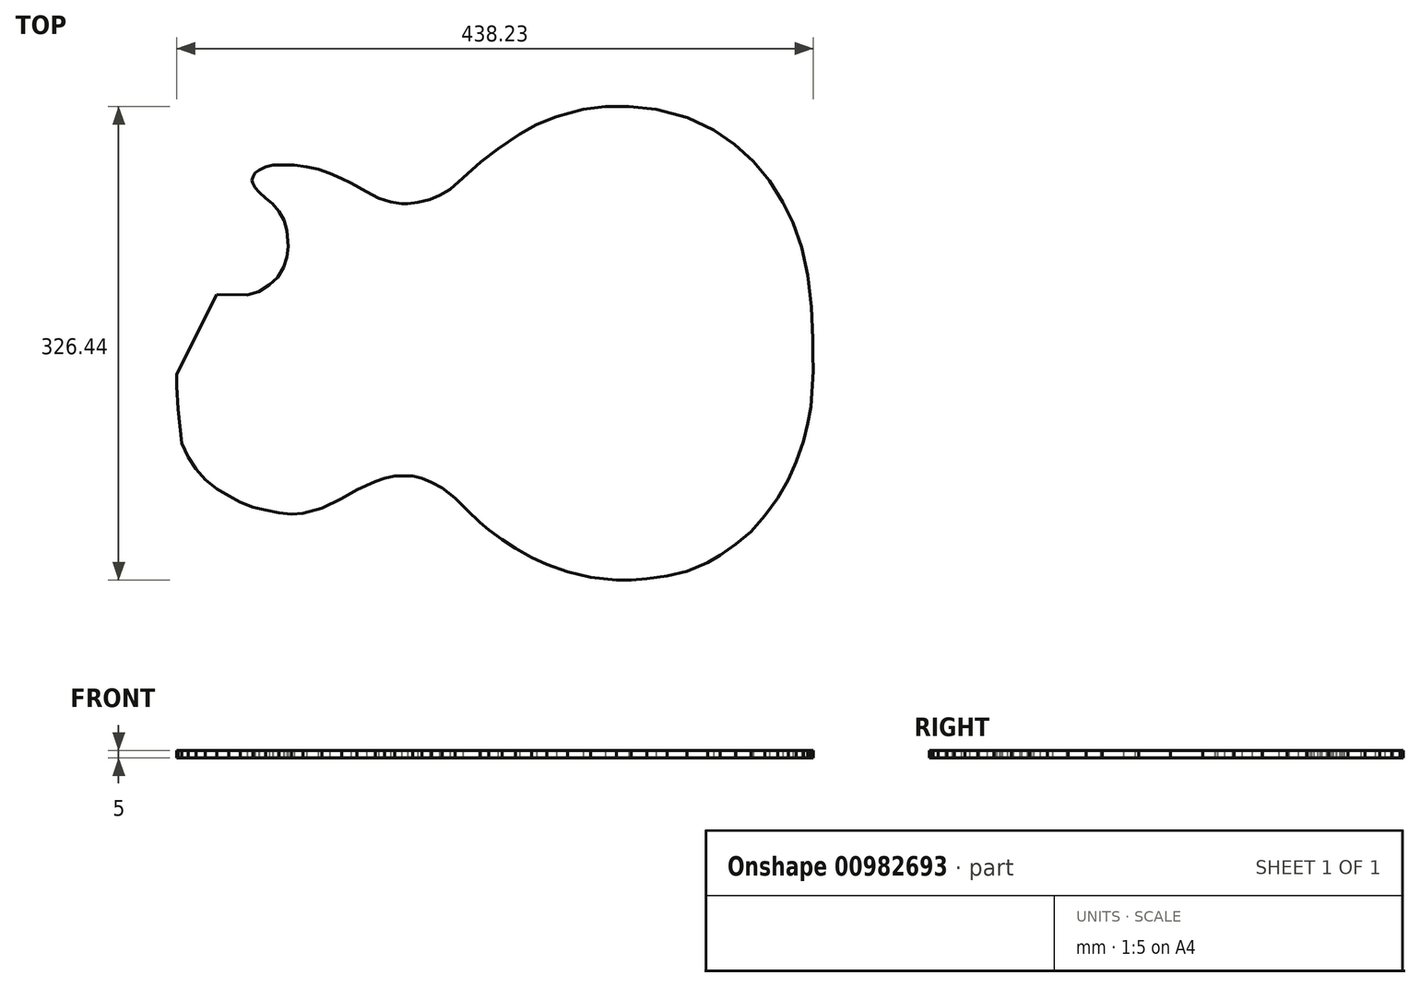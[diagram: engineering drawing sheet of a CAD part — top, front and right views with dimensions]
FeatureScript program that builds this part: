
annotation { "Feature Type Name" : "Feature", "Feature Type Description" : "" }
export const myFeature = defineFeature(function(context is Context, id is Id, definition is map)
    precondition{}
    {
        {
            var Q0;
            Q0=qCreatedBy(makeId("Top.planeOp"),FACE);
            var sketch = newSketch(context, id + "F0", { "sketchPlane" : qUnion([Q0])});
            skLineSegment(sketch, "E0", {"start": v(241.87, -9.5) * mm, "end": v(241.87, 1.22) * mm});
            skLineSegment(sketch, "E1", {"start": v(241.87, 1.22) * mm, "end": v(240.9, 23.4) * mm});
            skLineSegment(sketch, "E2", {"start": v(240.9, 23.4) * mm, "end": v(238.19, 45.15) * mm});
            skLineSegment(sketch, "E3", {"start": v(238.19, 45.15) * mm, "end": v(234.08, 64.4) * mm});
            skLineSegment(sketch, "E4", {"start": v(234.08, 64.4) * mm, "end": v(228.13, 81.5) * mm});
            skLineSegment(sketch, "E5", {"start": v(228.13, 81.5) * mm, "end": v(221.2, 95.35) * mm});
            skLineSegment(sketch, "E6", {"start": v(221.2, 95.35) * mm, "end": v(211.79, 110.28) * mm});
            skLineSegment(sketch, "E7", {"start": v(211.79, 110.28) * mm, "end": v(200.65, 123.59) * mm});
            skLineSegment(sketch, "E8", {"start": v(200.65, 123.59) * mm, "end": v(187.77, 135.38) * mm});
            skLineSegment(sketch, "E9", {"start": v(187.77, 135.38) * mm, "end": v(173.6, 145.23) * mm});
            skLineSegment(sketch, "E10", {"start": v(173.6, 145.23) * mm, "end": v(155.31, 153.78) * mm});
            skLineSegment(sketch, "E11", {"start": v(155.31, 153.78) * mm, "end": v(133.9, 159.4) * mm});
            skLineSegment(sketch, "E12", {"start": v(133.9, 159.4) * mm, "end": v(115.17, 161.46) * mm});
            skLineSegment(sketch, "E13", {"start": v(115.17, 161.46) * mm, "end": v(98.73, 161.46) * mm});
            skLineSegment(sketch, "E14", {"start": v(98.73, 161.46) * mm, "end": v(83.69, 159.4) * mm});
            skLineSegment(sketch, "E15", {"start": v(83.69, 159.4) * mm, "end": v(65.08, 154.53) * mm});
            skLineSegment(sketch, "E16", {"start": v(65.08, 154.53) * mm, "end": v(51.56, 148.9) * mm});
            skLineSegment(sketch, "E17", {"start": v(51.56, 148.9) * mm, "end": v(39.65, 142.3) * mm});
            skLineSegment(sketch, "E18", {"start": v(39.65, 142.3) * mm, "end": v(24.83, 132.35) * mm});
            skLineSegment(sketch, "E19", {"start": v(24.83, 132.35) * mm, "end": v(13.15, 123.37) * mm});
            skLineSegment(sketch, "E20", {"start": v(13.15, 123.37) * mm, "end": v(0.92, 112.23) * mm});
            skLineSegment(sketch, "E21", {"start": v(0.92, 112.23) * mm, "end": v(-8.28, 104.22) * mm});
            skLineSegment(sketch, "E22", {"start": v(-8.28, 104.22) * mm, "end": v(-15.42, 100) * mm});
            skLineSegment(sketch, "E23", {"start": v(-15.42, 100) * mm, "end": v(-22.02, 97.4) * mm});
            skLineSegment(sketch, "E24", {"start": v(-22.02, 97.4) * mm, "end": v(-30.35, 95.35) * mm});
            skLineSegment(sketch, "E25", {"start": v(-30.35, 95.35) * mm, "end": v(-37.23, 94.41) * mm});
            skLineSegment(sketch, "E26", {"start": v(-37.23, 94.41) * mm, "end": v(-41.61, 94.41) * mm});
            skLineSegment(sketch, "E27", {"start": v(-41.61, 94.41) * mm, "end": v(-49.08, 95.78) * mm});
            skLineSegment(sketch, "E28", {"start": v(-49.08, 95.78) * mm, "end": v(-57.2, 98.27) * mm});
            skLineSegment(sketch, "E29", {"start": v(-57.2, 98.27) * mm, "end": v(-65.74, 102.6) * mm});
            skLineSegment(sketch, "E30", {"start": v(-65.74, 102.6) * mm, "end": v(-76.46, 108.66) * mm});
            skLineSegment(sketch, "E31", {"start": v(-76.46, 108.66) * mm, "end": v(-83.17, 111.9) * mm});
            skLineSegment(sketch, "E32", {"start": v(-83.17, 111.9) * mm, "end": v(-91.06, 115.37) * mm});
            skLineSegment(sketch, "E33", {"start": v(-91.06, 115.37) * mm, "end": v(-99.07, 118.29) * mm});
            skLineSegment(sketch, "E34", {"start": v(-99.07, 118.29) * mm, "end": v(-106.86, 119.91) * mm});
            skLineSegment(sketch, "E35", {"start": v(-106.86, 119.91) * mm, "end": v(-115.52, 121) * mm});
            skLineSegment(sketch, "E36", {"start": v(-115.52, 121) * mm, "end": v(-123.64, 121) * mm});
            skLineSegment(sketch, "E37", {"start": v(-123.64, 121) * mm, "end": v(-129.91, 121) * mm});
            skLineSegment(sketch, "E38", {"start": v(-129.91, 121) * mm, "end": v(-135.21, 119.7) * mm});
            skLineSegment(sketch, "E39", {"start": v(-135.21, 119.7) * mm, "end": v(-139.65, 117.75) * mm});
            skLineSegment(sketch, "E40", {"start": v(-139.65, 117.75) * mm, "end": v(-142.36, 115.58) * mm});
            skLineSegment(sketch, "E41", {"start": v(-142.36, 115.58) * mm, "end": v(-143.66, 113.2) * mm});
            skLineSegment(sketch, "E42", {"start": v(-143.66, 113.2) * mm, "end": v(-144.74, 110.6) * mm});
            skLineSegment(sketch, "E43", {"start": v(-144.74, 110.6) * mm, "end": v(-143.98, 108.66) * mm});
            skLineSegment(sketch, "E44", {"start": v(-143.98, 108.66) * mm, "end": v(-142.46, 105.41) * mm});
            skLineSegment(sketch, "E45", {"start": v(-142.46, 105.41) * mm, "end": v(-139.54, 102.38) * mm});
            skLineSegment(sketch, "E46", {"start": v(-139.54, 102.38) * mm, "end": v(-135.21, 98.38) * mm});
            skLineSegment(sketch, "E47", {"start": v(-135.21, 98.38) * mm, "end": v(-130.45, 94.38) * mm});
            skLineSegment(sketch, "E48", {"start": v(-130.45, 94.38) * mm, "end": v(-125.8, 89.08) * mm});
            skLineSegment(sketch, "E49", {"start": v(-125.8, 89.08) * mm, "end": v(-122.34, 82.9) * mm});
            skLineSegment(sketch, "E50", {"start": v(-122.34, 82.9) * mm, "end": v(-120.5, 75.88) * mm});
            skLineSegment(sketch, "E51", {"start": v(-120.5, 75.88) * mm, "end": v(-119.55, 65) * mm});
            skLineSegment(sketch, "E52", {"start": v(-119.55, 65) * mm, "end": v(-120.52, 57.54) * mm});
            skLineSegment(sketch, "E53", {"start": v(-120.52, 57.54) * mm, "end": v(-121.78, 53.83) * mm});
            skLineSegment(sketch, "E54", {"start": v(-122.9, 50.5) * mm, "end": v(-127.02, 43.7) * mm});
            skLineSegment(sketch, "E55", {"start": v(-127.02, 43.7) * mm, "end": v(-132.75, 38.5) * mm});
            skLineSegment(sketch, "E56", {"start": v(-132.75, 38.5) * mm, "end": v(-140, 33.74) * mm});
            skLineSegment(sketch, "E57", {"start": v(-140, 33.74) * mm, "end": v(-147.93, 31.7) * mm});
            skLineSegment(sketch, "E58", {"start": v(-168.91, 31.93) * mm, "end": v(-196.33, -23.07) * mm});
            skLineSegment(sketch, "E59", {"start": v(-196.33, -23.07) * mm, "end": v(-196.33, -31.18) * mm});
            skLineSegment(sketch, "E60", {"start": v(-196.33, -31.18) * mm, "end": v(-195.5, -47.01) * mm});
            skLineSegment(sketch, "E61", {"start": v(-192.82, -70.53) * mm, "end": v(-188.49, -80.05) * mm});
            skLineSegment(sketch, "E62", {"start": v(-188.49, -80.05) * mm, "end": v(-182.97, -88.6) * mm});
            skLineSegment(sketch, "E63", {"start": v(-182.97, -88.6) * mm, "end": v(-176.58, -95.84) * mm});
            skLineSegment(sketch, "E64", {"start": v(-176.58, -95.84) * mm, "end": v(-168.91, -102.07) * mm});
            skLineSegment(sketch, "E65", {"start": v(-168.91, -102.07) * mm, "end": v(-160.5, -106.98) * mm});
            skLineSegment(sketch, "E66", {"start": v(-160.5, -106.98) * mm, "end": v(-152.64, -111.3) * mm});
            skLineSegment(sketch, "E67", {"start": v(-152.64, -111.3) * mm, "end": v(-143.87, -114.76) * mm});
            skLineSegment(sketch, "E68", {"start": v(-143.87, -114.76) * mm, "end": v(-135.21, -116.7) * mm});
            skLineSegment(sketch, "E69", {"start": v(-135.21, -116.7) * mm, "end": v(-125.92, -118.58) * mm});
            skLineSegment(sketch, "E70", {"start": v(-125.92, -118.58) * mm, "end": v(-117.41, -119.4) * mm});
            skLineSegment(sketch, "E71", {"start": v(-117.41, -119.4) * mm, "end": v(-109.47, -118.88) * mm});
            skLineSegment(sketch, "E72", {"start": v(-109.47, -118.88) * mm, "end": v(-96.26, -115.28) * mm});
            skLineSegment(sketch, "E73", {"start": v(-96.26, -115.28) * mm, "end": v(-82.63, -108.9) * mm});
            skLineSegment(sketch, "E74", {"start": v(-82.63, -108.9) * mm, "end": v(-72.35, -102.73) * mm});
            skLineSegment(sketch, "E75", {"start": v(-72.35, -102.73) * mm, "end": v(-59.47, -97.1) * mm});
            skLineSegment(sketch, "E76", {"start": v(-59.47, -97.1) * mm, "end": v(-53.09, -94.72) * mm});
            skLineSegment(sketch, "E77", {"start": v(-53.09, -94.72) * mm, "end": v(-46.27, -93.2) * mm});
            skLineSegment(sketch, "E78", {"start": v(-46.27, -93.2) * mm, "end": v(-39.78, -93.2) * mm});
            skLineSegment(sketch, "E79", {"start": v(-39.78, -93.2) * mm, "end": v(-33.72, -93.2) * mm});
            skLineSegment(sketch, "E80", {"start": v(-33.72, -93.2) * mm, "end": v(-27.55, -94.83) * mm});
            skLineSegment(sketch, "E81", {"start": v(-27.55, -94.83) * mm, "end": v(-20.73, -97.54) * mm});
            skLineSegment(sketch, "E82", {"start": v(-20.73, -97.54) * mm, "end": v(-13.7, -101.32) * mm});
            skLineSegment(sketch, "E83", {"start": v(-13.7, -101.32) * mm, "end": v(-4.72, -108.47) * mm});
            skLineSegment(sketch, "E84", {"start": v(-4.72, -108.47) * mm, "end": v(3.62, -116.58) * mm});
            skLineSegment(sketch, "E85", {"start": v(3.62, -116.58) * mm, "end": v(12.38, -125.13) * mm});
            skLineSegment(sketch, "E86", {"start": v(12.38, -125.13) * mm, "end": v(18.66, -130.43) * mm});
            skLineSegment(sketch, "E87", {"start": v(18.66, -130.43) * mm, "end": v(27.64, -137.14) * mm});
            skLineSegment(sketch, "E88", {"start": v(27.64, -137.14) * mm, "end": v(36.84, -142.98) * mm});
            skLineSegment(sketch, "E89", {"start": v(36.84, -142.98) * mm, "end": v(48.1, -149.25) * mm});
            skLineSegment(sketch, "E90", {"start": v(48.1, -149.25) * mm, "end": v(58.7, -154.12) * mm});
            skLineSegment(sketch, "E91", {"start": v(58.7, -154.12) * mm, "end": v(72.76, -159.2) * mm});
            skLineSegment(sketch, "E92", {"start": v(72.76, -159.2) * mm, "end": v(88.56, -163) * mm});
            skLineSegment(sketch, "E93", {"start": v(88.56, -163) * mm, "end": v(98.3, -164.08) * mm});
            skLineSegment(sketch, "E94", {"start": v(98.3, -164.08) * mm, "end": v(106.4, -164.98) * mm});
            skLineSegment(sketch, "E95", {"start": v(106.4, -164.98) * mm, "end": v(116.7, -164.98) * mm});
            skLineSegment(sketch, "E96", {"start": v(116.7, -164.98) * mm, "end": v(127.4, -164.08) * mm});
            skLineSegment(sketch, "E97", {"start": v(127.4, -164.08) * mm, "end": v(141.37, -162.24) * mm});
            skLineSegment(sketch, "E98", {"start": v(141.37, -162.24) * mm, "end": v(155, -158.78) * mm});
            skLineSegment(sketch, "E99", {"start": v(155, -158.78) * mm, "end": v(169.4, -152.82) * mm});
            skLineSegment(sketch, "E100", {"start": v(169.4, -152.82) * mm, "end": v(178.05, -147.74) * mm});
            skLineSegment(sketch, "E101", {"start": v(178.05, -147.74) * mm, "end": v(188.66, -140.27) * mm});
            skLineSegment(sketch, "E102", {"start": v(188.66, -140.27) * mm, "end": v(199.05, -131.62) * mm});
            skLineSegment(sketch, "E103", {"start": v(199.05, -131.62) * mm, "end": v(208.57, -120.47) * mm});
            skLineSegment(sketch, "E104", {"start": v(208.57, -120.47) * mm, "end": v(217.55, -108.36) * mm});
            skLineSegment(sketch, "E105", {"start": v(217.55, -108.36) * mm, "end": v(224.9, -95.8) * mm});
            skLineSegment(sketch, "E106", {"start": v(224.9, -95.8) * mm, "end": v(230.43, -83.47) * mm});
            skLineSegment(sketch, "E107", {"start": v(230.43, -83.47) * mm, "end": v(235.4, -69.2) * mm});
            skLineSegment(sketch, "E108", {"start": v(235.4, -69.2) * mm, "end": v(238.33, -56.86) * mm});
            skLineSegment(sketch, "E109", {"start": v(238.33, -56.86) * mm, "end": v(240.6, -45.6) * mm});
            skLineSegment(sketch, "E110", {"start": v(240.6, -45.6) * mm, "end": v(241.9, -20.83) * mm});
            skLineSegment(sketch, "E111", {"start": v(241.9, -20.83) * mm, "end": v(241.87, -9.5) * mm});
            skLineSegment(sketch, "E112", {"start": v(-168.91, 31.93) * mm, "end": v(-134.22, 31.56) * mm});
            skLineSegment(sketch, "E113", {"start": v(-113.15, 31.33) * mm, "end": v(-113.74, -23.8) * mm});
            skLineSegment(sketch, "E114", {"start": v(-196.33, -23.07) * mm, "end": v(-113.74, -23.8) * mm});
            skLineSegment(sketch, "E115.bottom", {"start": v(-105.24, 38.33) * mm, "end": v(-68.24, 38.33) * mm});
            skLineSegment(sketch, "E115.top", {"start": v(-105.24, -30.67) * mm, "end": v(-68.24, -30.67) * mm});
            skLineSegment(sketch, "E115.left", {"start": v(-105.24, 38.33) * mm, "end": v(-105.24, -30.67) * mm});
            skLineSegment(sketch, "E115.right", {"start": v(-68.24, 38.33) * mm, "end": v(-68.24, -30.67) * mm});
            skLineSegment(sketch, "E116.bottom", {"start": v(-2.24, 38.33) * mm, "end": v(34.76, 38.33) * mm});
            skLineSegment(sketch, "E116.top", {"start": v(-2.24, -30.67) * mm, "end": v(34.76, -30.67) * mm});
            skLineSegment(sketch, "E116.left", {"start": v(-2.24, 38.33) * mm, "end": v(-2.24, -30.67) * mm});
            skLineSegment(sketch, "E116.right", {"start": v(34.76, 38.33) * mm, "end": v(34.76, -30.67) * mm});
            skLineSegment(sketch, "E117.top", {"start": v(109.76, -47.01) * mm, "end": v(-195.5, -47.01) * mm});
            skLineSegment(sketch, "E117.left", {"start": v(109.76, 52.99) * mm, "end": v(109.76, -47.01) * mm});
            skLineSegment(sketch, "E118", {"start": v(-195.5, -47.01) * mm, "end": v(-192.82, -70.53) * mm});
            skLineSegment(sketch, "E119", {"start": v(-121.78, 53.83) * mm, "end": v(-122.9, 50.5) * mm});
            skLineSegment(sketch, "E120", {"start": v(-121.78, 53.83) * mm, "end": v(109.76, 52.99) * mm});
            skLineSegment(sketch, "E121.2", {"start": v(-123.11, 40.48) * mm, "end": v(-129.68, 34.53) * mm});
            skLineSegment(sketch, "E121.3", {"start": v(-118.34, 48.4) * mm, "end": v(-123.11, 40.48) * mm});
            skLineSegment(sketch, "E121.4", {"start": v(-117.04, 52.22) * mm, "end": v(-118.34, 48.4) * mm});
            skLineSegment(sketch, "E121.5", {"start": v(-115.63, 56.4) * mm, "end": v(-117.04, 52.22) * mm});
            skLineSegment(sketch, "E121.6", {"start": v(-114.52, 64.9) * mm, "end": v(-115.63, 56.4) * mm});
            skLineSegment(sketch, "E121.7", {"start": v(-115.55, 76.73) * mm, "end": v(-114.52, 64.9) * mm});
            skLineSegment(sketch, "E121.8", {"start": v(-117.66, 84.8) * mm, "end": v(-115.55, 76.73) * mm});
            skLineSegment(sketch, "E121.9", {"start": v(-121.7, 91.98) * mm, "end": v(-117.66, 84.8) * mm});
            skLineSegment(sketch, "E121.10", {"start": v(-126.95, 97.96) * mm, "end": v(-121.7, 91.98) * mm});
            skLineSegment(sketch, "E121.11", {"start": v(-131.9, 102.13) * mm, "end": v(-126.95, 97.96) * mm});
            skLineSegment(sketch, "E121.12", {"start": v(-136.04, 105.96) * mm, "end": v(-131.9, 102.13) * mm});
            skLineSegment(sketch, "E121.13", {"start": v(-138.29, 108.28) * mm, "end": v(-136.04, 105.96) * mm});
            skLineSegment(sketch, "E121.14", {"start": v(-139.34, 110.55) * mm, "end": v(-138.29, 108.28) * mm});
            skLineSegment(sketch, "E121.15", {"start": v(-139.14, 111.04) * mm, "end": v(-139.34, 110.55) * mm});
            skLineSegment(sketch, "E121.16", {"start": v(-138.45, 112.3) * mm, "end": v(-139.14, 111.04) * mm});
            skLineSegment(sketch, "E121.17", {"start": v(-137.04, 113.43) * mm, "end": v(-138.45, 112.3) * mm});
            skLineSegment(sketch, "E121.18", {"start": v(-133.6, 114.94) * mm, "end": v(-137.04, 113.43) * mm});
            skLineSegment(sketch, "E121.19", {"start": v(-129.3, 116) * mm, "end": v(-133.6, 114.94) * mm});
            skLineSegment(sketch, "E121.20", {"start": v(-123.64, 116) * mm, "end": v(-129.3, 116) * mm});
            skLineSegment(sketch, "E121.21", {"start": v(-115.83, 116) * mm, "end": v(-123.64, 116) * mm});
            skLineSegment(sketch, "E121.22", {"start": v(-107.68, 114.98) * mm, "end": v(-115.83, 116) * mm});
            skLineSegment(sketch, "E121.23", {"start": v(-100.45, 113.47) * mm, "end": v(-107.68, 114.98) * mm});
            skLineSegment(sketch, "E121.24", {"start": v(-92.93, 110.72) * mm, "end": v(-100.45, 113.47) * mm});
            skLineSegment(sketch, "E121.25", {"start": v(-85.26, 107.36) * mm, "end": v(-92.93, 110.72) * mm});
            skLineSegment(sketch, "E121.26", {"start": v(-78.78, 104.23) * mm, "end": v(-85.26, 107.36) * mm});
            skLineSegment(sketch, "E121.27", {"start": v(-68.1, 98.2) * mm, "end": v(-78.78, 104.23) * mm});
            skLineSegment(sketch, "E121.28", {"start": v(-59.07, 93.62) * mm, "end": v(-68.1, 98.2) * mm});
            skLineSegment(sketch, "E121.29", {"start": v(-50.27, 90.92) * mm, "end": v(-59.07, 93.62) * mm});
            skLineSegment(sketch, "E121.30", {"start": v(-42.07, 89.41) * mm, "end": v(-50.27, 90.92) * mm});
            skLineSegment(sketch, "E121.31", {"start": v(-36.9, 89.41) * mm, "end": v(-42.07, 89.41) * mm});
            skLineSegment(sketch, "E121.32", {"start": v(-29.4, 90.43) * mm, "end": v(-36.9, 89.41) * mm});
            skLineSegment(sketch, "E121.33", {"start": v(-20.5, 92.63) * mm, "end": v(-29.4, 90.43) * mm});
            skLineSegment(sketch, "E121.34", {"start": v(-13.22, 95.5) * mm, "end": v(-20.5, 92.63) * mm});
            skLineSegment(sketch, "E121.35", {"start": v(-5.34, 100.15) * mm, "end": v(-13.22, 95.5) * mm});
            skLineSegment(sketch, "E121.36", {"start": v(4.25, 108.5) * mm, "end": v(-5.34, 100.15) * mm});
            skLineSegment(sketch, "E121.37", {"start": v(16.36, 119.54) * mm, "end": v(4.25, 108.5) * mm});
            skLineSegment(sketch, "E121.38", {"start": v(27.75, 128.3) * mm, "end": v(16.36, 119.54) * mm});
            skLineSegment(sketch, "E121.39", {"start": v(42.26, 138.04) * mm, "end": v(27.75, 128.3) * mm});
            skLineSegment(sketch, "E121.40", {"start": v(213.37, -105.6) * mm, "end": v(220.46, -93.51) * mm});
            skLineSegment(sketch, "E121.41", {"start": v(204.65, -117.36) * mm, "end": v(213.37, -105.6) * mm});
            skLineSegment(sketch, "E121.42", {"start": v(195.52, -128.05) * mm, "end": v(204.65, -117.36) * mm});
            skLineSegment(sketch, "E121.43", {"start": v(185.61, -136.3) * mm, "end": v(195.52, -128.05) * mm});
            skLineSegment(sketch, "E121.44", {"start": v(175.34, -143.53) * mm, "end": v(185.61, -136.3) * mm});
            skLineSegment(sketch, "E121.45", {"start": v(167.16, -148.34) * mm, "end": v(175.34, -143.53) * mm});
            skLineSegment(sketch, "E121.46", {"start": v(153.42, -154.02) * mm, "end": v(167.16, -148.34) * mm});
            skLineSegment(sketch, "E121.47", {"start": v(140.42, -157.32) * mm, "end": v(153.42, -154.02) * mm});
            skLineSegment(sketch, "E121.48", {"start": v(126.87, -159.1) * mm, "end": v(140.42, -157.32) * mm});
            skLineSegment(sketch, "E121.49", {"start": v(116.49, -159.98) * mm, "end": v(126.87, -159.1) * mm});
            skLineSegment(sketch, "E121.50", {"start": v(106.68, -159.98) * mm, "end": v(116.49, -159.98) * mm});
            skLineSegment(sketch, "E121.51", {"start": v(98.85, -159.1) * mm, "end": v(106.68, -159.98) * mm});
            skLineSegment(sketch, "E121.52", {"start": v(21.77, -126.51) * mm, "end": v(30.48, -133.02) * mm});
            skLineSegment(sketch, "E121.53", {"start": v(15.74, -121.42) * mm, "end": v(21.77, -126.51) * mm});
            skLineSegment(sketch, "E121.54", {"start": v(7.1, -113) * mm, "end": v(15.74, -121.42) * mm});
            skLineSegment(sketch, "E121.55", {"start": v(-1.4, -104.7) * mm, "end": v(7.1, -113) * mm});
            skLineSegment(sketch, "E121.56", {"start": v(30.48, -133.02) * mm, "end": v(39.4, -138.68) * mm});
            skLineSegment(sketch, "E121.57", {"start": v(39.4, -138.68) * mm, "end": v(50.35, -144.8) * mm});
            skLineSegment(sketch, "E121.58", {"start": v(50.35, -144.8) * mm, "end": v(60.6, -149.5) * mm});
            skLineSegment(sketch, "E121.59", {"start": v(60.6, -149.5) * mm, "end": v(74.2, -154.41) * mm});
            skLineSegment(sketch, "E121.60", {"start": v(74.2, -154.41) * mm, "end": v(89.42, -158.06) * mm});
            skLineSegment(sketch, "E121.61", {"start": v(89.42, -158.06) * mm, "end": v(98.85, -159.1) * mm});
            skLineSegment(sketch, "E121.62", {"start": v(220.46, -93.51) * mm, "end": v(225.78, -81.63) * mm});
            skLineSegment(sketch, "E121.63", {"start": v(225.78, -81.63) * mm, "end": v(230.6, -67.79) * mm});
            skLineSegment(sketch, "E121.64", {"start": v(230.6, -67.79) * mm, "end": v(233.44, -55.79) * mm});
            skLineSegment(sketch, "E121.65", {"start": v(233.44, -55.79) * mm, "end": v(235.62, -44.98) * mm});
            skLineSegment(sketch, "E121.66", {"start": v(235.62, -44.98) * mm, "end": v(236.9, -20.7) * mm});
            skLineSegment(sketch, "E121.67", {"start": v(236.9, -20.7) * mm, "end": v(236.87, -9.51) * mm});
            skLineSegment(sketch, "E121.68", {"start": v(236.87, -9.51) * mm, "end": v(236.87, 1.11) * mm});
            skLineSegment(sketch, "E121.69", {"start": v(236.87, 1.11) * mm, "end": v(235.9, 22.98) * mm});
            skLineSegment(sketch, "E121.70", {"start": v(235.9, 22.98) * mm, "end": v(233.25, 44.32) * mm});
            skLineSegment(sketch, "E121.71", {"start": v(233.25, 44.32) * mm, "end": v(229.25, 63.06) * mm});
            skLineSegment(sketch, "E121.72", {"start": v(229.25, 63.06) * mm, "end": v(223.51, 79.55) * mm});
            skLineSegment(sketch, "E121.73", {"start": v(223.51, 79.55) * mm, "end": v(216.84, 92.9) * mm});
            skLineSegment(sketch, "E121.74", {"start": v(216.84, 92.9) * mm, "end": v(207.74, 107.33) * mm});
            skLineSegment(sketch, "E121.75", {"start": v(207.74, 107.33) * mm, "end": v(197.02, 120.13) * mm});
            skLineSegment(sketch, "E121.76", {"start": v(197.02, 120.13) * mm, "end": v(184.64, 131.47) * mm});
            skLineSegment(sketch, "E121.77", {"start": v(184.64, 131.47) * mm, "end": v(171.1, 140.88) * mm});
            skLineSegment(sketch, "E121.78", {"start": v(171.1, 140.88) * mm, "end": v(153.6, 149.05) * mm});
            skLineSegment(sketch, "E121.79", {"start": v(153.6, 149.05) * mm, "end": v(132.98, 154.47) * mm});
            skLineSegment(sketch, "E121.80", {"start": v(132.98, 154.47) * mm, "end": v(114.9, 156.46) * mm});
            skLineSegment(sketch, "E121.81", {"start": v(114.9, 156.46) * mm, "end": v(99.07, 156.46) * mm});
            skLineSegment(sketch, "E121.82", {"start": v(99.07, 156.46) * mm, "end": v(84.66, 154.49) * mm});
            skLineSegment(sketch, "E121.83", {"start": v(84.66, 154.49) * mm, "end": v(66.68, 149.78) * mm});
            skLineSegment(sketch, "E121.84", {"start": v(66.68, 149.78) * mm, "end": v(53.73, 144.4) * mm});
            skLineSegment(sketch, "E121.85", {"start": v(53.73, 144.4) * mm, "end": v(42.26, 138.04) * mm});
            skLineSegment(sketch, "E122.0", {"start": v(-10.94, -97.13) * mm, "end": v(-1.4, -104.7) * mm});
            skLineSegment(sketch, "E122.1", {"start": v(-18.62, -93) * mm, "end": v(-10.94, -97.13) * mm});
            skLineSegment(sketch, "E122.2", {"start": v(-25.99, -90.07) * mm, "end": v(-18.62, -93) * mm});
            skLineSegment(sketch, "E122.3", {"start": v(-33.07, -88.2) * mm, "end": v(-25.99, -90.07) * mm});
            skLineSegment(sketch, "E122.4", {"start": v(-39.78, -88.2) * mm, "end": v(-33.07, -88.2) * mm});
            skLineSegment(sketch, "E122.5", {"start": v(-110.3, -113.93) * mm, "end": v(-98, -110.57) * mm});
            skLineSegment(sketch, "E122.6", {"start": v(-117.34, -114.4) * mm, "end": v(-110.3, -113.93) * mm});
            skLineSegment(sketch, "E122.7", {"start": v(-125.18, -113.62) * mm, "end": v(-117.34, -114.4) * mm});
            skLineSegment(sketch, "E122.8", {"start": v(-134.17, -111.82) * mm, "end": v(-125.18, -113.62) * mm});
            skLineSegment(sketch, "E122.9", {"start": v(-98, -110.57) * mm, "end": v(-84.98, -104.48) * mm});
            skLineSegment(sketch, "E122.10", {"start": v(-84.98, -104.48) * mm, "end": v(-74.65, -98.28) * mm});
            skLineSegment(sketch, "E122.11", {"start": v(-74.65, -98.28) * mm, "end": v(-61.35, -92.47) * mm});
            skLineSegment(sketch, "E122.12", {"start": v(-61.35, -92.47) * mm, "end": v(-54.5, -89.92) * mm});
            skLineSegment(sketch, "E122.13", {"start": v(-54.5, -89.92) * mm, "end": v(-46.82, -88.2) * mm});
            skLineSegment(sketch, "E122.14", {"start": v(-46.82, -88.2) * mm, "end": v(-39.78, -88.2) * mm});
            skLineSegment(sketch, "E123.0", {"start": v(-142.4, -109.97) * mm, "end": v(-134.17, -111.82) * mm});
            skLineSegment(sketch, "E123.1", {"start": v(-150.5, -106.76) * mm, "end": v(-142.4, -109.97) * mm});
            skLineSegment(sketch, "E123.2", {"start": v(-158.03, -102.63) * mm, "end": v(-150.5, -106.76) * mm});
            skLineSegment(sketch, "E123.3", {"start": v(-166.06, -97.94) * mm, "end": v(-158.03, -102.63) * mm});
            skLineSegment(sketch, "E123.4", {"start": v(-173.1, -92.23) * mm, "end": v(-166.06, -97.94) * mm});
            skLineSegment(sketch, "E123.5", {"start": v(-190.47, -47.01) * mm, "end": v(-187.94, -69.18) * mm});
            skLineSegment(sketch, "E123.6", {"start": v(-187.94, -69.18) * mm, "end": v(-184.09, -77.64) * mm});
            skLineSegment(sketch, "E123.7", {"start": v(-184.09, -77.64) * mm, "end": v(-178.97, -85.57) * mm});
            skLineSegment(sketch, "E123.8", {"start": v(-178.97, -85.57) * mm, "end": v(-173.1, -92.23) * mm});
            skLineSegment(sketch, "E124", {"start": v(-134.22, 31.56) * mm, "end": v(-113.15, 31.33) * mm});
            skLineSegment(sketch, "E125", {"start": v(-129.68, 34.53) * mm, "end": v(-134.22, 31.56) * mm});
            skSolve(sketch);
        }
        {
            var Q0;
            {var subQ1=sQuery(id+"F0.wireOp",EDGE,"E117.left");Q0=makeQuery(id+"F0.imprint","IMPRINT",FACE,{"disambiguationData":[TD([[makeQuery(id+"F0.imprint","IMPRINT",EDGE,{"derivedFrom":subQ1}),1.0]])]});}
            var Q1;
            Q1=makeQuery(id+"F0.imprint","IMPRINT",FACE,{"disambiguationData":[TD([[makeQuery(id+"F0.imprint","IMPRINT",EDGE,{"derivedFrom":sQuery(id+"F0.wireOp",EDGE,"E0")}),1.0]])]});
            var Q2;
            Q2=makeQuery(id+"F0.imprint","IMPRINT",FACE,{"disambiguationData":[TD([[makeQuery(id+"F0.imprint","IMPRINT",EDGE,{"derivedFrom":sQuery(id+"F0.wireOp",EDGE,"E54")}),1.0]])]});
            var Q3;
            Q3=makeQuery(id+"F0.imprint","IMPRINT",FACE,{"disambiguationData":[TD([[makeQuery(id+"F0.imprint","IMPRINT",EDGE,{"derivedFrom":sQuery(id+"F0.wireOp",EDGE,"E59")}),1.0]])]});
            var Q4;
            {var subQ2=sQuery(id+"F0.wireOp",EDGE,"E58");Q4=makeQuery(id+"F0.imprint","IMPRINT",FACE,{"disambiguationData":[TD([[makeQuery(id+"F0.imprint","IMPRINT",EDGE,{"derivedFrom":subQ2}),1.0]])]});}
            var Q5;
            Q5=makeQuery(id+"F0.imprint","IMPRINT",FACE,{"disambiguationData":[TD([[makeQuery(id+"F0.imprint","IMPRINT",EDGE,{"derivedFrom":sQuery(id+"F0.wireOp",EDGE,"E115.bottom")}),-1.0]])]});
            var Q6;
            Q6=makeQuery(id+"F0.imprint","IMPRINT",FACE,{"disambiguationData":[TD([[makeQuery(id+"F0.imprint","IMPRINT",EDGE,{"derivedFrom":sQuery(id+"F0.wireOp",EDGE,"E116.bottom")}),-1.0]])]});
            extrude(context, id + "F1", {"entities" : qUnion([Q0, Q1, Q2, Q3, Q4, Q5, Q6]), "depth" : 5 * mm, "offsetDistance" : 25 * mm});
        }
    });
